# Revit family: Domotics-DomesticRanges-GEWISS-CHORUS_POWER-SOCKET-OUTLET_ITADEU_P30_16A
name_source: partatom
category: Apparecchi elettrici
revit_build: Autodesk Revit 2016 (Build: 20161004_0715(x64)
units: mm (PartAtom-declared; Revit-internal decimal feet)

## family parameters
Condiviso = Sì
Host = Superficie
Mantenere orientamento annotazione = Sì
Numero OmniClass = 23.80.50.14
Punto di calcolo locali = No
Quota connettore circolare = Usa diametro
Taglio con vuoti quando caricato = Sì
Tipo di parte = Normale
Titolo OmniClass = Plug Connectors

## types (3) — shared parameters
Breaking capacity: = 1.25 In (100 position changes)
Catalogue = DOMOTICS
Catalogue Range = CHORUS - DOMESTIC RANGE
Characteristics = With safety shields
Description: = 2P+E - 16A
Earth pit = Side and central
Electrocod = 0131
For plug pins = Ã˜ 4 / 4.8 mm
GW - Testo Elettrico = UNIV.
Glow Wire Test = 850°C
IDF = 2708ae5f-4db8-49eb-bc6d-5fb6d0f939dd
IDT = 4361459a-fdcf-4cc1-be1a-a7e1343b0a22
Immagine tipo = GW14205.jpg
Insulation resistance = > 5 MOhm
Larghezza presa = 46 mm  [stored 0.150919 ft]
No. Chorus modules = 2
No. Chorus modules: = 2
Offset bidimensionale7 = 2 mm  [stored 0.00656168 ft]
Produttore = GEWISS S.p.A.
Prolonged operation (no.of position changes) = 10.000 at In 250 V ac cosÃ˜=0,8
Prospetto di default = 1219 mm
Resistance at test voltage = 2000 V at 50 Hz for 1 minute
SEO = Socket outlet
Simbolo_ = SIMBOLO PRESE : PRESA
Socket-out type = P30
Standard = Italian / German
Standard: = Italian / German
Standard; = IEC 60884-1
Technical sheet = https://www.gewiss.com
Terminal grip on cable traction = > 50 N
Terminal tightening capacity flexible cables (mm2) = min. 0,75 - max. 2x4
Terminal tightening capacity rigid cables (mm2) = min. 0,5 - max. 2x2,5
Thermo-pressure with ball = 125
Tipo_ = CHORUS PRESE ITAGER P30 16A_BASE : TITANIO
Type = P30
URL = https://www.gewiss.com
Version file RFA = 19.0
Voltage = 250 V ac
Voltage: = 250 V ac
Wiring terminals = With screw

## per-type parameters (varying)
| type | Category | Colour | Description. | Descrizione | EAN code | Modello |
| GW12205 - Black | Dual amperage socket-outlet | Black | Dual amperage socket-outlet | SOCKET, 2M 2P+E 16A P30 IT/G ST BLACK | 8011564266902 | GW12205 |
| GW14205 - Titanium | Dual amperage socket-outlet | Titanium | Dual amperage socket-outlet | SOCKET 2M 2P+E 16A P30 IT/G ST TITANIUM | 8011564266322 | GW14205 |
| GW10205 - White | Socket-outlet | White | Socket-outlet | S. OUT. 2M 2P+EARTH 16A P30 IT/DE ST WH | 8011564257948 | GW10205 |

note: source unit labels omitted for Thermo-pressure with ball — the stored unit's dimension contradicts the parameter name (converter mislabeling)

note: [stored X ft] marks values corroborated as IEEE doubles in the binary element streams (Revit-internal decimal feet)

## geometry (parser evidence)
native form markers: Sweep x2
no freeform markers — native parametric forms only
